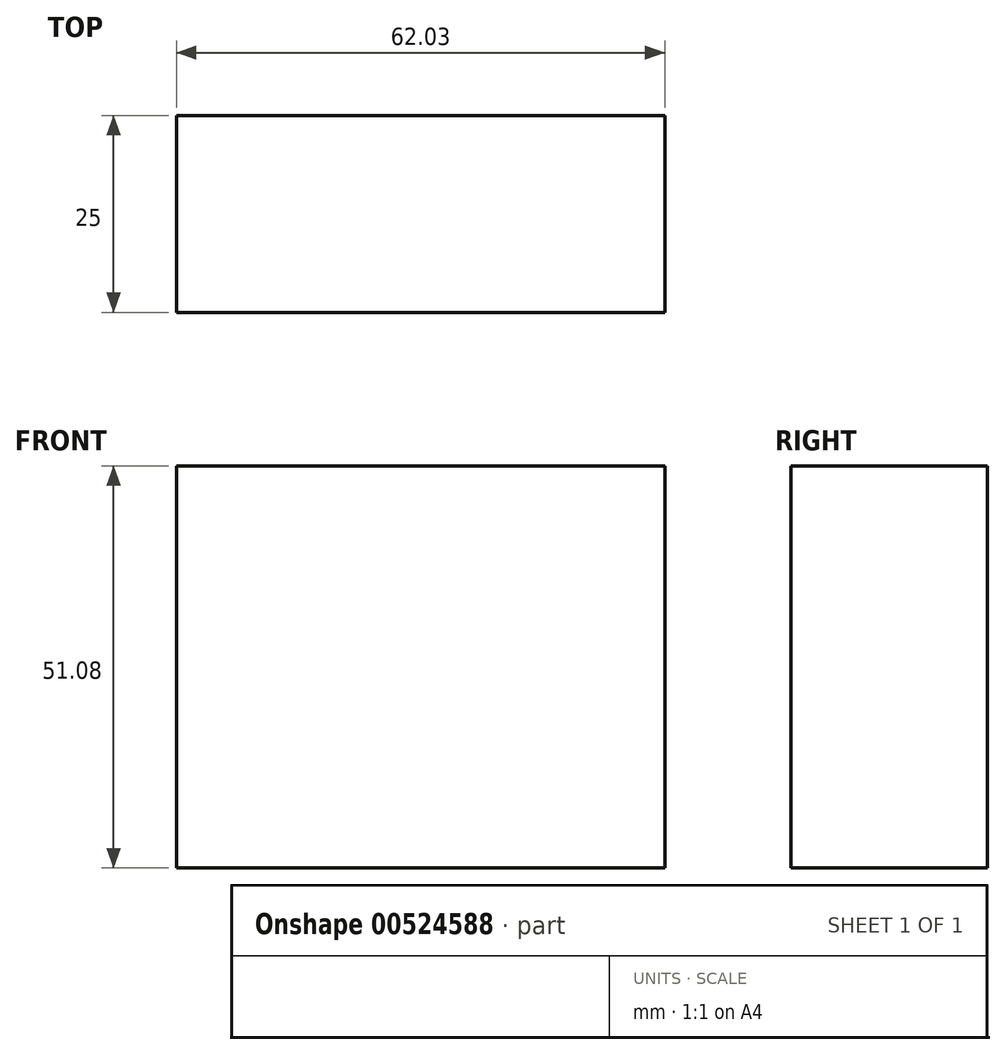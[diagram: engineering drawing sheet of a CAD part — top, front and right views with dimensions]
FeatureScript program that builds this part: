
annotation { "Feature Type Name" : "Feature", "Feature Type Description" : "" }
export const myFeature = defineFeature(function(context is Context, id is Id, definition is map)
    precondition{}
    {
        {
            var Q0;
            Q0=qCreatedBy(makeId("Front.planeOp"),FACE);
            var sketch = newSketch(context, id + "F0", { "sketchPlane" : qUnion([Q0])});
            skLineSegment(sketch, "E0.bottom", {"start": v(28.3, 26.47) * mm, "end": v(-33.73, 26.47) * mm});
            skLineSegment(sketch, "E0.top", {"start": v(28.3, -24.6) * mm, "end": v(-33.73, -24.6) * mm});
            skLineSegment(sketch, "E0.left", {"start": v(28.3, 26.47) * mm, "end": v(28.3, -24.6) * mm});
            skLineSegment(sketch, "E0.right", {"start": v(-33.73, 26.47) * mm, "end": v(-33.73, -24.6) * mm});
            skSolve(sketch);
        }
        {
            var Q0;
            Q0=makeQuery(id+"F0.imprint","IMPRINT",FACE,{"disambiguationData":[TD([[makeQuery(id+"F0.imprint","IMPRINT",EDGE,{"derivedFrom":sQuery(id+"F0.wireOp",EDGE,"E0.bottom")}),1.0]])]});
            extrude(context, id + "F1", {"entities" : qUnion([Q0]), "depth" : 25 * mm, "offsetDistance" : 25 * mm});
        }
    });
